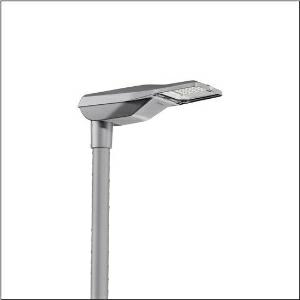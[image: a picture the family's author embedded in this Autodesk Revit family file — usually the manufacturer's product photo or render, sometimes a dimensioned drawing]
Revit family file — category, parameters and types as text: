
# Revit family: streetlight_sl_21_iq_micro___st1_5a_5xe1p41d08cb_4bae
name_source: partatom
category: Lighting Fixtures
units: mm (PartAtom-declared; Revit-internal decimal feet)

## family parameters
Cut with Voids When Loaded = No
Host = Face
Light Source = No
Part Type = Normal
Room Calculation Point = No
Round Connector Dimension = Use Diameter
Shared = No

## types (1)
- --- (1 x LED, 2930 lm, 19.4 W, 4000K)
    Apparent Load = 19 VA
    CIE Flux Codes = 22 53 95 100 100
    Color Rendering = 70
    Color Temperature = 4000K
    Default Elevation = 1800 mm
    Description = Streetlight SL 21 iQ micro, mast luminaire, primary light control with lens, of PMMA, primary optical cover: cover, of toughened safety glass, transparent, light distribution: ST1.5a, light emission: direct distribution, primary light characteristic: asymmetric, installation type: post-top, side-entry, LED, High Power LED, rated luminous flux: 2.930lm, luminous efficacy: 151lm/W, light colour: 740, colour temperature: 4000K, control gear: iQ-Comfort, control: Auto-Match, Temp-Guard, Lumen-Switch, Night-Set, Smart-Wire, Light-Fading, Desk-Remote (wireless, voltage-free reading and setting of iQ features in the workshop via application-optimized NFC function/RFID function), optimised constant luminous flux control (CLO 2.0), pre-setting: linear dimming characteristic, mains connection: 220..240V, AC, 50/60Hz, start of lifetime: 19W, end of service life: 20W, reduction: 10W, luminaire housing, of diecast aluminium, powder-coated, Siteco® metallic grey (DB 702S), corrosivity category C5 mid according to DIN EN ISO 12944, please order mast flange separately, inclination adjustable: 0°, 5°, 10°, 15°, sealing non-destructively replaceable, multi-level sealing system, length: 528mm, width: 235mm, height: 110mm, mast flange for spigot size: 42mm (side-entry): 5XC10008XM4, 60/48mm (side-entry/post-top): 5XC10108XM2, 76/60mm (side-entry/post-top): 5XC10108XM1, protection rating (complete): IP66, insulation class (complete): insulation class II (safety insulation), certification: CE, ENEC, ENEC+, VDE, impact resistance: IK10, permissible operating ambient temperature for outdoor applications: -40..+50°C, standard-compliant lighting for roads and squares, packaging unit: 1 piece

Light Distribution: ST1.5a
    Height = 110 mm
    Lamp = 1 x LED
    Lamp Light Flux = 2930 lm
    Lamp Power = 19.4 W
    Lamp count = 1
    Length = 528 mm
    Luminous efficacy = 151 lm/W
    Manufacturer = Siteco
    ModVariant = No
    Model = 5XE1P41D08CB
    Number of Poles = 1
    OnlyDefault = Yes
    Power Factor = 1
    Product Name = Streetlight SL 21 iQ micro | ST1.5a
    Product group = mast luminaire | pylon top
    ProductGroupID = 6100
    Protection Class = Protection class II
    Protection Degree = IP 66
    RLX_Detail_Level = 1
    RLX_Emergency_Light_Flux = 0 lm
    RLX_Emergency_Type = 0
    RLX_Emergency_Type_DB = No
    RlxData = <blob elided: 103893 chars, md5=c462ba9d>
    Socket = socket
    Standby Power = 0 W
    System Light Flux = 2930 lm
    System Power = 19 W
    Type Comments = factory setting: luminous flux: 100 % | dim-lin: 254 | 387 mA
    Type Image = l_1006881.jpg
    URL = http://relux.com
    VarID = @adj_159515
    Voltage = 0 V
    Weight = 0.00 kg
    Width = 235 mm

## geometry (parser evidence)
native form markers: Blend x4, Sweep x13
no freeform markers — native parametric forms only
